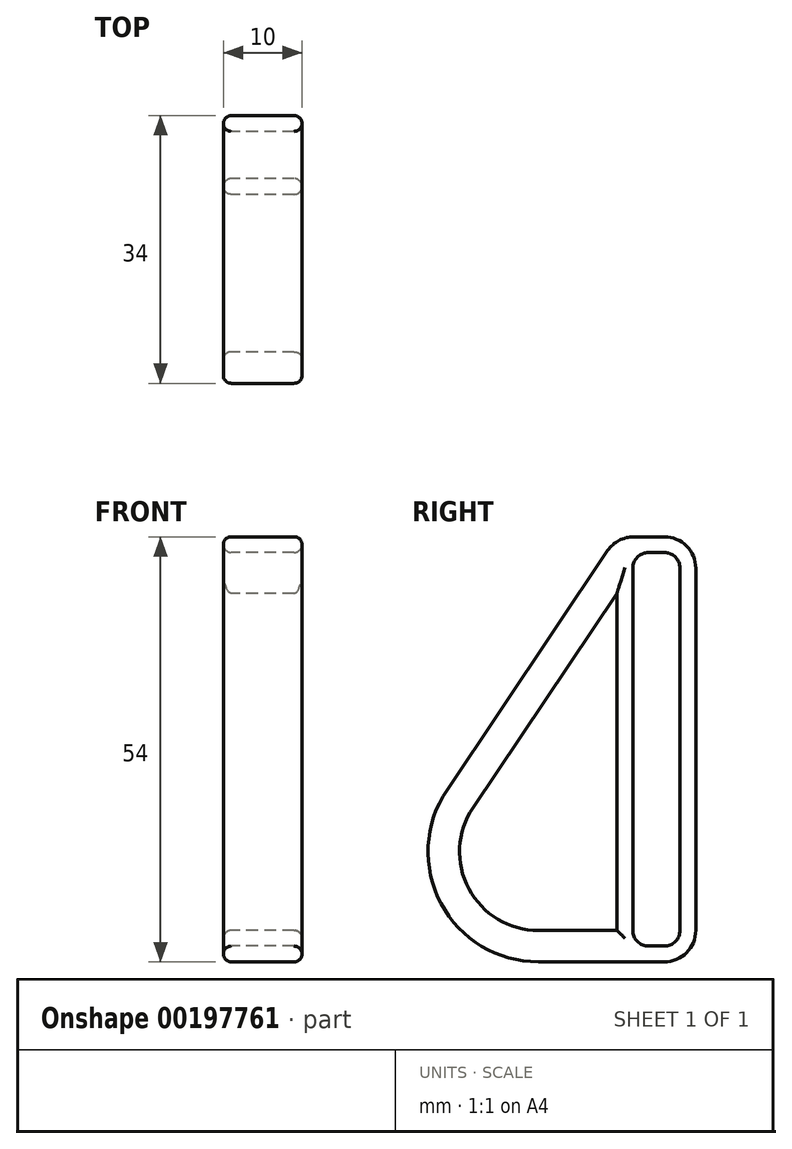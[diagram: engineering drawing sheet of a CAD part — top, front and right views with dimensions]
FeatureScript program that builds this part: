
annotation { "Feature Type Name" : "Feature", "Feature Type Description" : "" }
export const myFeature = defineFeature(function(context is Context, id is Id, definition is map)
    precondition{}
    {
        {
            assignVariable(context, id + "F0", {"name" : "LOOP_WIDTH", "anyValue" : 10});
        }
        {
            assignVariable(context, id + "F1", {"name" : "THICKNESS", "anyValue" : 2});
        }
        {
            var Q0;
            Q0=qCreatedBy(makeId("Right.planeOp"),FACE);
            var sketch = newSketch(context, id + "F2", { "sketchPlane" : qUnion([Q0])});
            skLineSegment(sketch, "E0", {"start": v(0, 54) * mm, "end": v(10, 54) * mm});
            skLineSegment(sketch, "E1", {"start": v(10, 54) * mm, "end": v(10, 0) * mm});
            skLineSegment(sketch, "E2", {"start": v(10, 0) * mm, "end": v(0, 0) * mm});
            skLineSegment(sketch, "E3", {"start": v(0, 0) * mm, "end": v(0, 54) * mm});
            skLineSegment(sketch, "E4", {"start": v(8, 2) * mm, "end": v(8, 52) * mm});
            skLineSegment(sketch, "E5", {"start": v(8, 52) * mm, "end": v(2, 52) * mm});
            skLineSegment(sketch, "E6", {"start": v(2, 2) * mm, "end": v(8, 2) * mm});
            skLineSegment(sketch, "E7", {"start": v(2, 52) * mm, "end": v(2, 2) * mm});
            skSolve(sketch);
        }
        {
            var Q0;
            Q0=qSketchRegion(id+"F2",true);
            extrude(context, id + "F3", {"entities" : qUnion([Q0]), "endBound" : BoundingType.SYMMETRIC, "depth" : (getVariable(context, 'LOOP_WIDTH')) * mm});
        }
        {
            var Q0;
            Q0=qCreatedBy(makeId("Right.planeOp"),FACE);
            var sketch = newSketch(context, id + "F4", { "sketchPlane" : qUnion([Q0])});
            skLineSegment(sketch, "E8", {"start": v(0, 4) * mm, "end": v(-10, 4) * mm});
            skArc(sketch, "E9.filletArc", {"start": v(-18.3, 19.58) * mm, "mid": v(-18.82, 9.3) * mm, "end": v(-10, 4) * mm});
            skLineSegment(sketch, "E10", {"start": v(-18.3, 19.58) * mm, "end": v(0, 46.83) * mm});
            skArc(sketch, "E11", {"start": v(-18.3, 19.58) * mm, "mid": v(-1.18, 18.7) * mm, "end": v(-10, 4) * mm, "construction": true});
            skArc(sketch, "E12", {"start": v(-10, 0) * mm, "mid": v(-22.35, 7.42) * mm, "end": v(-21.62, 21.8) * mm});
            skLineSegment(sketch, "E13", {"start": v(-21.62, 21.8) * mm, "end": v(0, 54) * mm});
            skLineSegment(sketch, "E14", {"start": v(0, 54) * mm, "end": v(0, 46.83) * mm});
            skLineSegment(sketch, "E15", {"start": v(-10, 0) * mm, "end": v(0, 0) * mm});
            skLineSegment(sketch, "E16", {"start": v(0, 0) * mm, "end": v(0, 4) * mm});
            skSolve(sketch);
        }
        {
            var Q0;
            Q0 = qSketchRegion(id + "F4", true);
            extrude(context, id + "F5", {"entities" : qUnion([Q0]), "operationType" : NewBodyOperationType.ADD, "endBound" : BoundingType.SYMMETRIC, "depth" : (getVariable(context, 'LOOP_WIDTH')) * mm});
        }
        {
            var Q0;
            Q0=makeQuery(id+"F3.opExtrude","SWEPT_EDGE",EDGE,{"disambiguationData":[OSD([sQuery(id+"F2.wireOp",EDGE,"E0"),sQuery(id+"F2.wireOp",EDGE,"E1")])]});
            var Q1;
            Q1=makeQuery(id+"F5.boolean.opBoolean","MERGE",EDGE,{"derivedFrom":[makeQuery(id+"F3.opExtrude","SWEPT_EDGE",EDGE,{"disambiguationData":[OSD([sQuery(id+"F2.wireOp",EDGE,"E0"),sQuery(id+"F2.wireOp",EDGE,"E3")])]}),makeQuery(id+"F5.opExtrude","SWEPT_EDGE",EDGE,{"disambiguationData":[OSD([sQuery(id+"F4.wireOp",EDGE,"E13"),sQuery(id+"F4.wireOp",EDGE,"E14")])]})]});
            var Q2;
            Q2=makeQuery(id+"F3.opExtrude","SWEPT_EDGE",EDGE,{"disambiguationData":[OSD([sQuery(id+"F2.wireOp",EDGE,"E1"),sQuery(id+"F2.wireOp",EDGE,"E2")])]});
            fillet(context, id + "F6", {"entities" : qUnion([Q0, Q1, Q2]), "radius" : (getVariable(context, 'THICKNESS') * 2) * mm, "tangentPropagation" : true, "allowEdgeOverflow" : false});
        }
        {
            var Q0;
            Q0=makeQuery(id+"F3.opExtrude","SWEPT_EDGE",EDGE,{"disambiguationData":[OSD([sQuery(id+"F2.wireOp",EDGE,"E4"),sQuery(id+"F2.wireOp",EDGE,"E5")])]});
            var Q1;
            Q1=makeQuery(id+"F3.opExtrude","SWEPT_EDGE",EDGE,{"disambiguationData":[OSD([sQuery(id+"F2.wireOp",EDGE,"E5"),sQuery(id+"F2.wireOp",EDGE,"E7")])]});
            var Q2;
            Q2=makeQuery(id+"F3.opExtrude","SWEPT_EDGE",EDGE,{"disambiguationData":[OSD([sQuery(id+"F2.wireOp",EDGE,"E4"),sQuery(id+"F2.wireOp",EDGE,"E6")])]});
            var Q3;
            Q3=makeQuery(id+"F3.opExtrude","SWEPT_EDGE",EDGE,{"disambiguationData":[OSD([sQuery(id+"F2.wireOp",EDGE,"E6"),sQuery(id+"F2.wireOp",EDGE,"E7")])]});
            var Q4;
            Q4=makeQuery(id+"F5.opExtrude","SWEPT_EDGE",EDGE,{"disambiguationData":[OSD([sQuery(id+"F4.wireOp",EDGE,"E8"),sQuery(id+"F4.wireOp",EDGE,"E16")])]});
            var Q5;
            Q5=makeQuery(id+"F5.opExtrude","SWEPT_EDGE",EDGE,{"disambiguationData":[OSD([sQuery(id+"F4.wireOp",EDGE,"E10"),sQuery(id+"F4.wireOp",EDGE,"E14")])]});
            fillet(context, id + "F7", {"entities" : qUnion([Q0, Q1, Q2, Q3, Q4, Q5]), "radius" : (getVariable(context, 'THICKNESS')) * mm, "tangentPropagation" : true, "allowEdgeOverflow" : false});
        }
        {
            var Q0;
            Q0=makeQuery(id+"F5.boolean.opBoolean","MERGE",FACE,{"derivedFrom":[makeQuery(id+"F3.opExtrude","CAP_FACE",FACE,{"disambiguationData":[OSD([sQuery(id+"F2.wireOp",EDGE,"E0"),sQuery(id+"F2.wireOp",EDGE,"E1"),sQuery(id+"F2.wireOp",EDGE,"E2"),sQuery(id+"F2.wireOp",EDGE,"E3"),sQuery(id+"F2.wireOp",EDGE,"E4"),sQuery(id+"F2.wireOp",EDGE,"E5"),sQuery(id+"F2.wireOp",EDGE,"E6"),sQuery(id+"F2.wireOp",EDGE,"E7")])],"isStart":false}),makeQuery(id+"F5.opExtrude","CAP_FACE",FACE,{"disambiguationData":[OSD([sQuery(id+"F4.wireOp",EDGE,"E8"),sQuery(id+"F4.wireOp",EDGE,"E9.filletArc"),sQuery(id+"F4.wireOp",EDGE,"E10"),sQuery(id+"F4.wireOp",EDGE,"E12"),sQuery(id+"F4.wireOp",EDGE,"E13"),sQuery(id+"F4.wireOp",EDGE,"E14"),sQuery(id+"F4.wireOp",EDGE,"E15"),sQuery(id+"F4.wireOp",EDGE,"E16")])],"isStart":false})]});
            var Q1;
            Q1=makeQuery(id+"F5.boolean.opBoolean","MERGE",FACE,{"derivedFrom":[makeQuery(id+"F3.opExtrude","CAP_FACE",FACE,{"disambiguationData":[OSD([sQuery(id+"F2.wireOp",EDGE,"E0"),sQuery(id+"F2.wireOp",EDGE,"E1"),sQuery(id+"F2.wireOp",EDGE,"E2"),sQuery(id+"F2.wireOp",EDGE,"E3"),sQuery(id+"F2.wireOp",EDGE,"E4"),sQuery(id+"F2.wireOp",EDGE,"E5"),sQuery(id+"F2.wireOp",EDGE,"E6"),sQuery(id+"F2.wireOp",EDGE,"E7")])],"isStart":true}),makeQuery(id+"F5.opExtrude","CAP_FACE",FACE,{"disambiguationData":[OSD([sQuery(id+"F4.wireOp",EDGE,"E8"),sQuery(id+"F4.wireOp",EDGE,"E9.filletArc"),sQuery(id+"F4.wireOp",EDGE,"E10"),sQuery(id+"F4.wireOp",EDGE,"E12"),sQuery(id+"F4.wireOp",EDGE,"E13"),sQuery(id+"F4.wireOp",EDGE,"E14"),sQuery(id+"F4.wireOp",EDGE,"E15"),sQuery(id+"F4.wireOp",EDGE,"E16")])],"isStart":true})]});
            fillet(context, id + "F8", {"entities" : qUnion([Q0, Q1]), "radius" : (getVariable(context, 'THICKNESS') / 2) * mm, "tangentPropagation" : true, "allowEdgeOverflow" : false});
        }
    });
